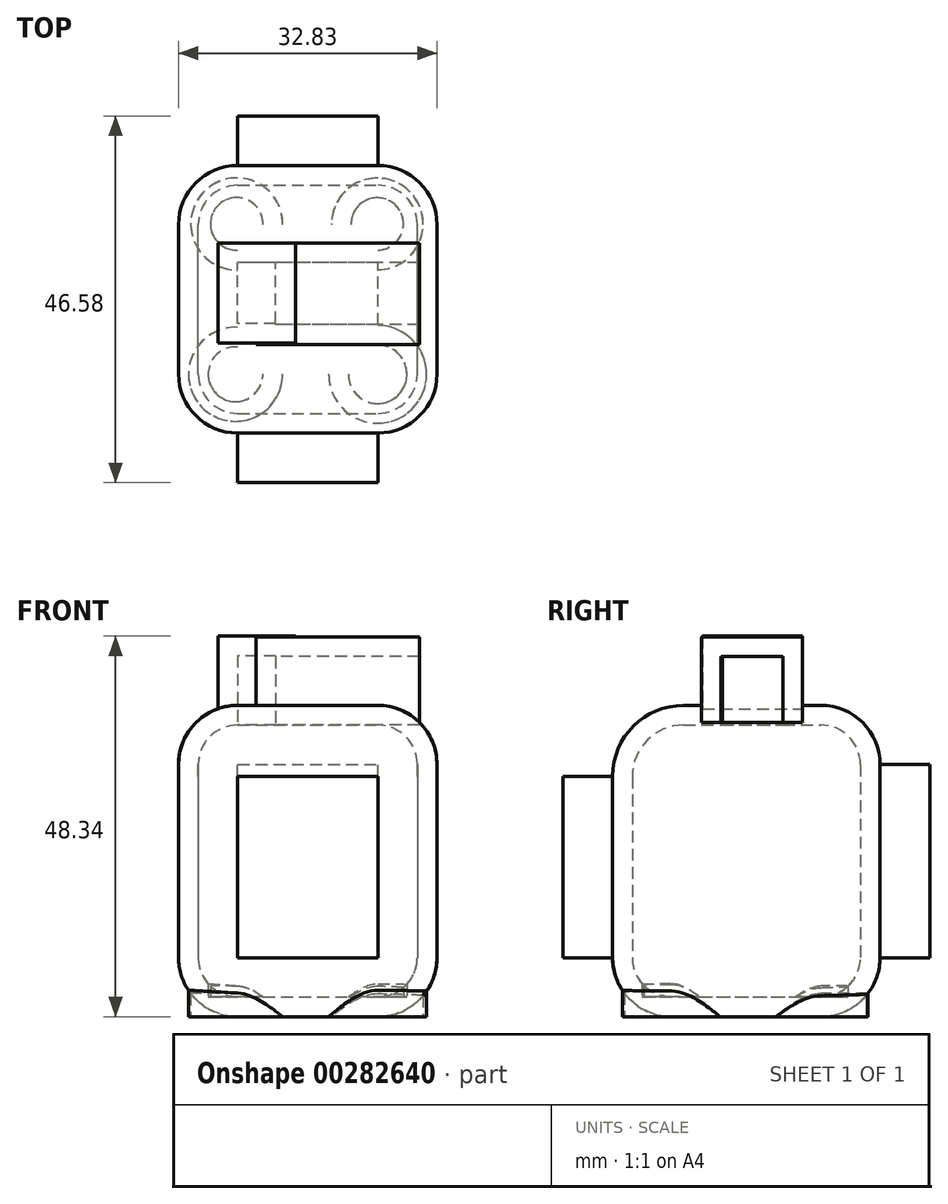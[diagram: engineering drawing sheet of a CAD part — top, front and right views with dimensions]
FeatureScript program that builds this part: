
annotation { "Feature Type Name" : "Feature", "Feature Type Description" : "" }
export const myFeature = defineFeature(function(context is Context, id is Id, definition is map)
    precondition{}
    {
        {
            var Q0;
            Q0=qCreatedBy(makeId("Top.planeOp"),FACE);
            var sketch = newSketch(context, id + "F0", { "sketchPlane" : qUnion([Q0])});
            skLineSegment(sketch, "E0.bottom", {"start": v(0, 0) * mm, "end": v(27.83, 0) * mm});
            skLineSegment(sketch, "E0.top", {"start": v(0, 28.98) * mm, "end": v(27.83, 28.98) * mm});
            skLineSegment(sketch, "E0.left", {"start": v(0, 0) * mm, "end": v(0, 28.98) * mm});
            skLineSegment(sketch, "E0.right", {"start": v(27.83, 0) * mm, "end": v(27.83, 28.98) * mm});
            skSolve(sketch);
        }
        {
            var Q0;
            Q0=makeQuery(id+"F0.imprint","IMPRINT",FACE,{"disambiguationData":[TD([[makeQuery(id+"F0.imprint","IMPRINT",EDGE,{"derivedFrom":sQuery(id+"F0.wireOp",EDGE,"E0.bottom")}),1.0]])]});
            extrude(context, id + "F1", {"entities" : qUnion([Q0]), "depth" : 34.54 * mm});
        }
        {
            var Q0;
            Q0=makeQuery(id+"F1.opExtrude","CAP_EDGE",EDGE,{"disambiguationData":[OSD([sQuery(id+"F0.wireOp",EDGE,"E0.bottom")])],"isStart":false});
            fillet(context, id + "F2", {"entities" : qUnion([Q0]), "radius" : 6.52 * mm, "tangentPropagation" : true, "allowEdgeOverflow" : false});
        }
        {
            var Q0;
            Q0=makeQuery(id+"F1.opExtrude","CAP_EDGE",EDGE,{"disambiguationData":[OSD([sQuery(id+"F0.wireOp",EDGE,"E0.bottom")])],"isStart":true});
            fillet(context, id + "F3", {"entities" : qUnion([Q0]), "radius" : 5 * mm, "tangentPropagation" : true, "allowEdgeOverflow" : false});
        }
        {
            var Q0;
            Q0=makeQuery(id+"F1.opExtrude","CAP_EDGE",EDGE,{"disambiguationData":[OSD([sQuery(id+"F0.wireOp",EDGE,"E0.left")])],"isStart":true});
            var Q1;
            Q1=makeQuery(id+"F1.opExtrude","SWEPT_EDGE",EDGE,{"disambiguationData":[OSD([sQuery(id+"F0.wireOp",EDGE,"E0.top"),sQuery(id+"F0.wireOp",EDGE,"E0.left")])]});
            var Q2;
            Q2=makeQuery(id+"F1.opExtrude","CAP_EDGE",EDGE,{"disambiguationData":[OSD([sQuery(id+"F0.wireOp",EDGE,"E0.top")])],"isStart":true});
            var Q3;
            Q3=makeQuery(id+"F1.opExtrude","CAP_EDGE",EDGE,{"disambiguationData":[OSD([sQuery(id+"F0.wireOp",EDGE,"E0.right")])],"isStart":true});
            var Q4;
            Q4=makeQuery(id+"F1.opExtrude","SWEPT_EDGE",EDGE,{"disambiguationData":[OSD([sQuery(id+"F0.wireOp",EDGE,"E0.top"),sQuery(id+"F0.wireOp",EDGE,"E0.right")])]});
            var Q5;
            Q5=makeQuery(id+"F1.opExtrude","CAP_EDGE",EDGE,{"disambiguationData":[OSD([sQuery(id+"F0.wireOp",EDGE,"E0.top")])],"isStart":false});
            fillet(context, id + "F4", {"entities" : qUnion([Q0, Q1, Q2, Q3, Q4, Q5]), "radius" : 5 * mm, "tangentPropagation" : true, "allowEdgeOverflow" : false});
        }
        {
            var Q0;
            Q0=qCreatedBy(makeId("Top.planeOp"),FACE);
            var sketch = newSketch(context, id + "F5", { "sketchPlane" : qUnion([Q0])});
            skCircle(sketch, "E1", {"center": v(4.74, 4.96) * mm, "radius": 3.47 * mm});
            skCircle(sketch, "E2", {"center": v(22.8, 4.96) * mm, "radius": 3.72 * mm});
            skCircle(sketch, "E3", {"center": v(4.89, 24.07) * mm, "radius": 3.34 * mm});
            skCircle(sketch, "E4", {"center": v(22.75, 24.07) * mm, "radius": 3.32 * mm});
            skSolve(sketch);
        }
        {
            var Q0;
            Q0=makeQuery(id+"F5.imprint","IMPRINT",FACE,{"disambiguationData":[TD([[makeQuery(id+"F5.imprint","IMPRINT",EDGE,{"derivedFrom":sQuery(id+"F5.wireOp",EDGE,"E1")}),1.0]])]});
            var Q1;
            Q1=makeQuery(id+"F5.imprint","IMPRINT",FACE,{"disambiguationData":[TD([[makeQuery(id+"F5.imprint","IMPRINT",EDGE,{"derivedFrom":sQuery(id+"F5.wireOp",EDGE,"E2")}),1.0]])]});
            var Q2;
            Q2=makeQuery(id+"F5.imprint","IMPRINT",FACE,{"disambiguationData":[TD([[makeQuery(id+"F5.imprint","IMPRINT",EDGE,{"derivedFrom":sQuery(id+"F5.wireOp",EDGE,"E3")}),1.0]])]});
            var Q3;
            Q3=makeQuery(id+"F5.imprint","IMPRINT",FACE,{"disambiguationData":[TD([[makeQuery(id+"F5.imprint","IMPRINT",EDGE,{"derivedFrom":sQuery(id+"F5.wireOp",EDGE,"E4")}),1.0]])]});
            extrude(context, id + "F6", {"entities" : qUnion([Q0, Q1, Q2, Q3]), "operationType" : NewBodyOperationType.ADD, "depth" : 25 * mm});
        }
        {
            var Q0;
            Q0=makeQuery(id+"F1.opExtrude","CAP_FACE",FACE,{"disambiguationData":[OSD([sQuery(id+"F0.wireOp",EDGE,"E0.bottom"),sQuery(id+"F0.wireOp",EDGE,"E0.top"),sQuery(id+"F0.wireOp",EDGE,"E0.left"),sQuery(id+"F0.wireOp",EDGE,"E0.right")])],"isStart":false});
            var sketch = newSketch(context, id + "F7", { "sketchPlane" : qUnion([Q0])});
            skLineSegment(sketch, "E5.bottom", {"start": v(18, 11.27) * mm, "end": v(9.83, 11.27) * mm});
            skLineSegment(sketch, "E5.top", {"start": v(18, 19.14) * mm, "end": v(9.83, 19.14) * mm});
            skLineSegment(sketch, "E5.left", {"start": v(18, 11.27) * mm, "end": v(18, 19.14) * mm});
            skLineSegment(sketch, "E5.right", {"start": v(9.83, 11.27) * mm, "end": v(9.83, 19.14) * mm});
            skPoint(sketch, "E5.middle", {"position": v(13.91, 15.2) * mm});
            skPoint(sketch, "E5.middle.positionSnap0", {"position": v(13.91, 23.98) * mm});
            skPoint(sketch, "E5.centerSnap0", {"position": v(13.91, 23.98) * mm});
            skSolve(sketch);
        }
        {
            var Q0;
            Q0=makeQuery(id+"F7.imprint","IMPRINT",FACE,{"disambiguationData":[TD([[makeQuery(id+"F7.imprint","IMPRINT",EDGE,{"derivedFrom":sQuery(id+"F7.wireOp",EDGE,"E5.bottom")}),-1.0]])]});
            extrude(context, id + "F8", {"entities" : qUnion([Q0]), "operationType" : NewBodyOperationType.ADD, "depth" : 8.7 * mm});
        }
        {
            var Q0;
            Q0=makeQuery(id+"F8.opExtrude","SWEPT_FACE",FACE,{"disambiguationData":[OSD([sQuery(id+"F7.wireOp",EDGE,"E5.left")])]});
            extrude(context, id + "F9", {"entities" : qUnion([Q0]), "operationType" : NewBodyOperationType.ADD, "depth" : 10.1 * mm});
        }
        {
            var Q0;
            Q0=makeQuery(id+"F1.opExtrude","CAP_FACE",FACE,{"disambiguationData":[OSD([sQuery(id+"F0.wireOp",EDGE,"E0.bottom"),sQuery(id+"F0.wireOp",EDGE,"E0.top"),sQuery(id+"F0.wireOp",EDGE,"E0.left"),sQuery(id+"F0.wireOp",EDGE,"E0.right")])],"isStart":false});
            var sketch = newSketch(context, id + "F10", { "sketchPlane" : qUnion([Q0])});
            skLineSegment(sketch, "E6.bottom", {"start": v(9.83, 19.14) * mm, "end": v(5, 19.14) * mm});
            skLineSegment(sketch, "E6.top", {"start": v(9.83, 11.43) * mm, "end": v(5, 11.43) * mm});
            skLineSegment(sketch, "E6.left", {"start": v(9.83, 19.14) * mm, "end": v(9.83, 11.43) * mm});
            skLineSegment(sketch, "E6.right", {"start": v(5, 19.14) * mm, "end": v(5, 11.43) * mm});
            skSolve(sketch);
        }
        {
            var Q0;
            Q0 = qSketchRegion(id + "F10", true);
            extrude(context, id + "F11", {"entities" : qUnion([Q0]), "operationType" : NewBodyOperationType.ADD, "depth" : 8.8 * mm});
        }
        {
            var Q0;
            Q0=makeQuery(id+"F9.opExtrude","CAP_FACE",FACE,{"disambiguationData":[OSD([sQuery(id+"F7.wireOp",EDGE,"E5.left")])],"isStart":false});
            shell(context, id + "F12", {"entities" : qUnion([Q0]), "thickness" : 2.5 * mm, "oppositeDirection" : true});
        }
        {
            var Q0;
            Q0=makeQuery(id+"F1.opExtrude","SWEPT_FACE",FACE,{"disambiguationData":[OSD([sQuery(id+"F0.wireOp",EDGE,"E0.bottom")])]});
            extrude(context, id + "F13", {"entities" : qUnion([Q0]), "operationType" : NewBodyOperationType.ADD, "depth" : 6.3 * mm});
        }
        {
            var Q0;
            Q0=makeQuery(id+"F1.opExtrude","SWEPT_FACE",FACE,{"disambiguationData":[OSD([sQuery(id+"F0.wireOp",EDGE,"E0.top")])]});
            extrude(context, id + "F14", {"entities" : qUnion([Q0]), "operationType" : NewBodyOperationType.ADD, "depth" : 6.3 * mm});
        }
    });
